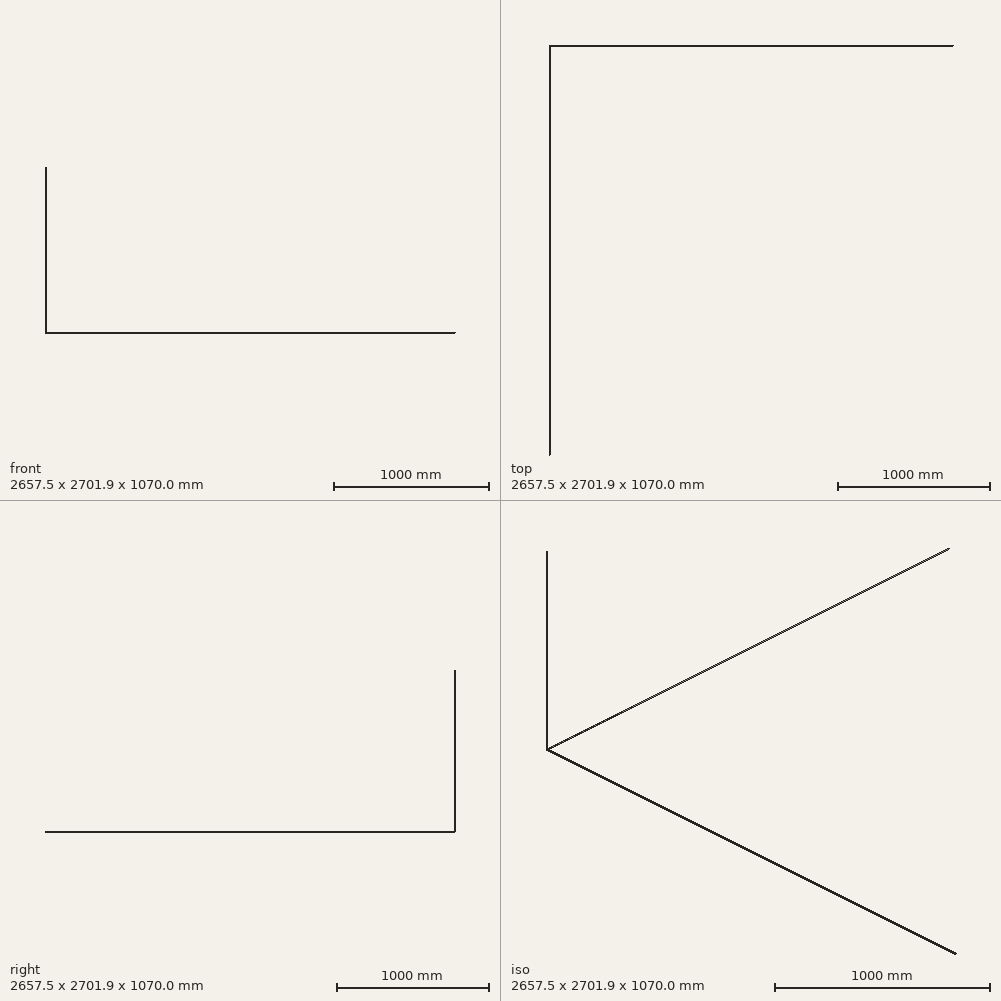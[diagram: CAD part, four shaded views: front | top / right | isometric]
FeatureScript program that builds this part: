
annotation { "Feature Type Name" : "Feature", "Feature Type Description" : "" }
export const myFeature = defineFeature(function(context is Context, id is Id, definition is map)
    precondition{}
    {
        {
            var Q0;
            Q0=qCreatedBy(makeId("Right.planeOp"),FACE);
            var sketch = newSketch(context, id + "F0", { "sketchPlane" : qUnion([Q0])});
            skCircle(sketch, "E0", {"center": v(0, 0) * mm, "radius": 3.18 * mm});
            skSolve(sketch);
        }
        {
            var Q0;
            Q0=makeQuery(id+"F0.imprint","IMPRINT",FACE,{"disambiguationData":[TD([[makeQuery(id+"F0.imprint","IMPRINT",EDGE,{"derivedFrom":sQuery(id+"F0.wireOp",EDGE,"E0")}),1.0]])]});
            extrude(context, id + "F1", {"entities" : qUnion([Q0]), "depth" : 2654.3 * mm, "offsetDistance" : 25.4 * mm});
        }
        {
            var Q0;
            Q0=qCreatedBy(makeId("Right.planeOp"),FACE);
            var sketch = newSketch(context, id + "F2", { "sketchPlane" : qUnion([Q0])});
            skCircle(sketch, "E1", {"center": v(0, 0) * mm, "radius": 3.18 * mm});
            skSolve(sketch);
        }
        {
            var Q0;
            Q0=makeQuery(id+"F2.imprint","IMPRINT",FACE,{"disambiguationData":[TD([[makeQuery(id+"F2.imprint","IMPRINT",EDGE,{"derivedFrom":sQuery(id+"F2.wireOp",EDGE,"E1")}),1.0]])]});
            extrude(context, id + "F3", {"entities" : qUnion([Q0]), "depth" : 565.15 * mm, "offsetDistance" : 25.4 * mm});
        }
        {
            var Q0;
            Q0=qCreatedBy(makeId("Front.planeOp"),FACE);
            var sketch = newSketch(context, id + "F4", { "sketchPlane" : qUnion([Q0])});
            skCircle(sketch, "E2", {"center": v(0, 0) * mm, "radius": 3.18 * mm});
            skSolve(sketch);
        }
        {
            var Q0;
            Q0=makeQuery(id+"F4.imprint","IMPRINT",FACE,{"disambiguationData":[TD([[makeQuery(id+"F4.imprint","IMPRINT",EDGE,{"derivedFrom":sQuery(id+"F4.wireOp",EDGE,"E2")}),1.0]])]});
            extrude(context, id + "F5", {"entities" : qUnion([Q0]), "depth" : 1238.25 * mm, "offsetDistance" : 25.4 * mm});
        }
        {
            var Q0;
            Q0=qCreatedBy(makeId("Front.planeOp"),FACE);
            var sketch = newSketch(context, id + "F6", { "sketchPlane" : qUnion([Q0])});
            skCircle(sketch, "E3", {"center": v(0, 0) * mm, "radius": 3.17 * mm});
            skSolve(sketch);
        }
        {
            var Q0;
            Q0=makeQuery(id+"F6.imprint","IMPRINT",FACE,{"disambiguationData":[TD([[makeQuery(id+"F6.imprint","IMPRINT",EDGE,{"derivedFrom":sQuery(id+"F6.wireOp",EDGE,"E3")}),1.0]])]});
            extrude(context, id + "F7", {"entities" : qUnion([Q0]), "depth" : 1282.7 * mm, "offsetDistance" : 25.4 * mm});
        }
        {
            var Q0;
            Q0=qCreatedBy(makeId("Front.planeOp"),FACE);
            var sketch = newSketch(context, id + "F8", { "sketchPlane" : qUnion([Q0])});
            skCircle(sketch, "E4", {"center": v(0, 0) * mm, "radius": 3.18 * mm});
            skSolve(sketch);
        }
        {
            var Q0;
            Q0=makeQuery(id+"F8.imprint","IMPRINT",FACE,{"disambiguationData":[TD([[makeQuery(id+"F8.imprint","IMPRINT",EDGE,{"derivedFrom":sQuery(id+"F8.wireOp",EDGE,"E4")}),1.0]])]});
            extrude(context, id + "F9", {"entities" : qUnion([Q0]), "depth" : 2698.75 * mm, "offsetDistance" : 25.4 * mm});
        }
        {
            var Q0;
            Q0=qCreatedBy(makeId("Front.planeOp"),FACE);
            var sketch = newSketch(context, id + "F10", { "sketchPlane" : qUnion([Q0])});
            skCircle(sketch, "E5", {"center": v(0, 0) * mm, "radius": 3.18 * mm});
            skSolve(sketch);
        }
        {
            var Q0;
            Q0=makeQuery(id+"F10.imprint","IMPRINT",FACE,{"disambiguationData":[TD([[makeQuery(id+"F10.imprint","IMPRINT",EDGE,{"derivedFrom":sQuery(id+"F10.wireOp",EDGE,"E5")}),1.0]])]});
            extrude(context, id + "F11", {"entities" : qUnion([Q0]), "depth" : 1258.57 * mm, "offsetDistance" : 25.4 * mm});
        }
        {
            var Q0;
            Q0=qCreatedBy(makeId("Top.planeOp"),FACE);
            var sketch = newSketch(context, id + "F12", { "sketchPlane" : qUnion([Q0])});
            skCircle(sketch, "E6", {"center": v(0, 0) * mm, "radius": 3.18 * mm});
            skSolve(sketch);
        }
        {
            var Q0;
            Q0=makeQuery(id+"F12.imprint","IMPRINT",FACE,{"disambiguationData":[TD([[makeQuery(id+"F12.imprint","IMPRINT",EDGE,{"derivedFrom":sQuery(id+"F12.wireOp",EDGE,"E6")}),1.0]])]});
            extrude(context, id + "F13", {"entities" : qUnion([Q0]), "depth" : 914.4 * mm, "offsetDistance" : 25.4 * mm});
        }
        {
            var Q0;
            Q0=qCreatedBy(makeId("Top.planeOp"),FACE);
            var sketch = newSketch(context, id + "F14", { "sketchPlane" : qUnion([Q0])});
            skCircle(sketch, "E7", {"center": v(0, 0) * mm, "radius": 3.18 * mm});
            skSolve(sketch);
        }
        {
            var Q0;
            Q0=makeQuery(id+"F14.imprint","IMPRINT",FACE,{"disambiguationData":[TD([[makeQuery(id+"F14.imprint","IMPRINT",EDGE,{"derivedFrom":sQuery(id+"F14.wireOp",EDGE,"E7")}),1.0]])]});
            extrude(context, id + "F15", {"entities" : qUnion([Q0]), "depth" : 1066.8 * mm, "offsetDistance" : 25.4 * mm});
        }
        {
            var Q0;
            Q0=qCreatedBy(makeId("Top.planeOp"),FACE);
            var sketch = newSketch(context, id + "F16", { "sketchPlane" : qUnion([Q0])});
            skCircle(sketch, "E8", {"center": v(0, 0) * mm, "radius": 3.18 * mm});
            skSolve(sketch);
        }
        {
            var Q0;
            Q0=makeQuery(id+"F16.imprint","IMPRINT",FACE,{"disambiguationData":[TD([[makeQuery(id+"F16.imprint","IMPRINT",EDGE,{"derivedFrom":sQuery(id+"F16.wireOp",EDGE,"E8")}),1.0]])]});
            extrude(context, id + "F17", {"entities" : qUnion([Q0]), "depth" : 996.95 * mm, "offsetDistance" : 25.4 * mm});
        }
    });
